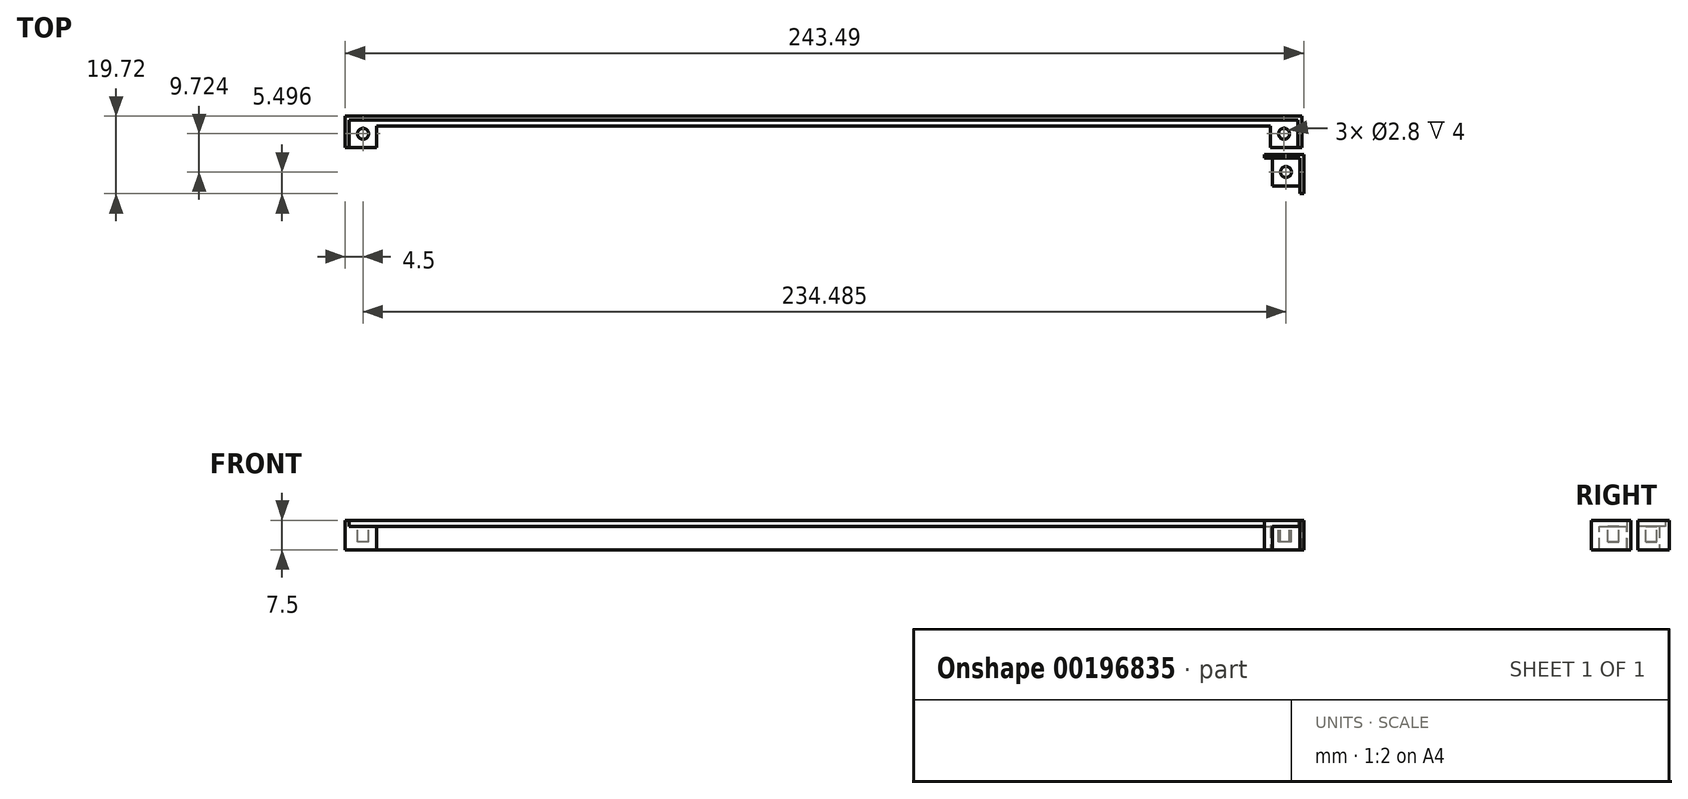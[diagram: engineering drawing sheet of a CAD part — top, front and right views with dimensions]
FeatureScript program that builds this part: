
annotation { "Feature Type Name" : "Feature", "Feature Type Description" : "" }
export const myFeature = defineFeature(function(context is Context, id is Id, definition is map)
    precondition{}
    {
        {
            var Q0;
            Q0=qCreatedBy(makeId("Top.planeOp"),FACE);
            var sketch = newSketch(context, id + "F0", { "sketchPlane" : qUnion([Q0])});
            skLineSegment(sketch, "E0.bottom", {"start": v(121.5, -4) * mm, "end": v(113.5, -4) * mm});
            skLineSegment(sketch, "E0.top", {"start": v(121.5, 4) * mm, "end": v(-121.5, 4) * mm});
            skLineSegment(sketch, "E0.left", {"start": v(121.5, -4) * mm, "end": v(121.5, 4) * mm});
            skLineSegment(sketch, "E0.right", {"start": v(-121.5, -4) * mm, "end": v(-121.5, 4) * mm});
            skPoint(sketch, "E0.middle", {"position": v(0, 0) * mm});
            skLineSegment(sketch, "E1.bottom", {"start": v(-113.5, 1.5) * mm, "end": v(113.5, 1.5) * mm});
            skLineSegment(sketch, "E1.left", {"start": v(-113.5, 1.5) * mm, "end": v(-113.5, -4) * mm});
            skLineSegment(sketch, "E1.right", {"start": v(113.5, 1.5) * mm, "end": v(113.5, -4) * mm});
            skLineSegment(sketch, "E2.trimOffspring", {"start": v(-113.5, -4) * mm, "end": v(-121.5, -4) * mm});
            skSolve(sketch);
        }
        {
            var Q0;
            Q0 = qSketchRegion(id + "F0", true);
            extrude(context, id + "F1", {"entities" : qUnion([Q0]), "depth" : 6 * mm});
        }
        {
            var Q0;
            Q0=makeQuery(id+"F1.opExtrude","CAP_FACE",FACE,{"disambiguationData":[OSD([sQuery(id+"F0.wireOp",EDGE,"E0.bottom"),sQuery(id+"F0.wireOp",EDGE,"E0.top"),sQuery(id+"F0.wireOp",EDGE,"E0.left"),sQuery(id+"F0.wireOp",EDGE,"E0.right")])],"isStart":false});
            var sketch = newSketch(context, id + "F2", { "sketchPlane" : qUnion([Q0])});
            skCircle(sketch, "E3", {"center": v(-117, -0.5) * mm, "radius": 1.4 * mm});
            skCircle(sketch, "E4", {"center": v(117, -0.5) * mm, "radius": 1.4 * mm});
            skSolve(sketch);
        }
        {
            var Q0;
            Q0 = qSketchRegion(id + "F2", true);
            extrude(context, id + "F3", {"entities" : qUnion([Q0]), "operationType" : NewBodyOperationType.REMOVE, "oppositeDirection" : true, "depth" : 4 * mm});
        }
        {
            var Q0;
            Q0=makeQuery(id+"F1.opExtrude","CAP_FACE",FACE,{"disambiguationData":[OSD([sQuery(id+"F0.wireOp",EDGE,"E0.bottom"),sQuery(id+"F0.wireOp",EDGE,"E0.top"),sQuery(id+"F0.wireOp",EDGE,"E0.left"),sQuery(id+"F0.wireOp",EDGE,"E0.right"),sQuery(id+"F0.wireOp",EDGE,"E1.bottom"),sQuery(id+"F0.wireOp",EDGE,"E1.left"),sQuery(id+"F0.wireOp",EDGE,"E1.right"),sQuery(id+"F0.wireOp",EDGE,"E2.trimOffspring")])],"isStart":false});
            var sketch = newSketch(context, id + "F4", { "sketchPlane" : qUnion([Q0])});
            skLineSegment(sketch, "E5", {"start": v(-121.5, 4) * mm, "end": v(-121.5, -4) * mm});
            skLineSegment(sketch, "E6", {"start": v(-121.5, -4) * mm, "end": v(-120.5, -4) * mm});
            skLineSegment(sketch, "E7", {"start": v(-120.5, -4) * mm, "end": v(-120.5, 3) * mm});
            skLineSegment(sketch, "E8", {"start": v(-120.5, 3) * mm, "end": v(120.5, 3) * mm});
            skLineSegment(sketch, "E9", {"start": v(120.5, 3) * mm, "end": v(120.5, -4) * mm});
            skLineSegment(sketch, "E10", {"start": v(120.5, -4) * mm, "end": v(121.5, -4) * mm});
            skLineSegment(sketch, "E11", {"start": v(121.5, -4) * mm, "end": v(121.5, 4) * mm});
            skLineSegment(sketch, "E12", {"start": v(121.5, 4) * mm, "end": v(-121.5, 4) * mm});
            skSolve(sketch);
        }
        {
            var Q0;
            Q0 = qSketchRegion(id + "F4", true);
            extrude(context, id + "F5", {"entities" : qUnion([Q0]), "operationType" : NewBodyOperationType.ADD, "depth" : 1.5 * mm});
        }
        {
            var Q0;
            Q0=qCreatedBy(makeId("Top.planeOp"),FACE);
            var sketch = newSketch(context, id + "F6", { "sketchPlane" : qUnion([Q0])});
            skLineSegment(sketch, "E13.bottom", {"start": v(111.99, -5.72) * mm, "end": v(121.99, -5.72) * mm});
            skLineSegment(sketch, "E13.top", {"start": v(111.99, -15.72) * mm, "end": v(121.99, -15.72) * mm});
            skLineSegment(sketch, "E13.left", {"start": v(111.99, -5.72) * mm, "end": v(111.99, -15.72) * mm});
            skLineSegment(sketch, "E13.right", {"start": v(121.99, -5.72) * mm, "end": v(121.99, -15.72) * mm});
            skSolve(sketch);
        }
        {
            var Q0;
            Q0 = qSketchRegion(id + "F6", true);
            extrude(context, id + "F7", {"entities" : qUnion([Q0]), "depth" : 6 * mm});
        }
        {
            var Q0;
            Q0=makeQuery(id+"F7.opExtrude","CAP_FACE",FACE,{"disambiguationData":[OSD([sQuery(id+"F6.wireOp",EDGE,"E13.bottom"),sQuery(id+"F6.wireOp",EDGE,"E13.top"),sQuery(id+"F6.wireOp",EDGE,"E13.left"),sQuery(id+"F6.wireOp",EDGE,"E13.right")])],"isStart":false});
            var sketch = newSketch(context, id + "F8", { "sketchPlane" : qUnion([Q0])});
            skCircle(sketch, "E14", {"center": v(117.49, -10.22) * mm, "radius": 1.4 * mm});
            skSolve(sketch);
        }
        {
            var Q0;
            Q0 = qSketchRegion(id + "F8", true);
            extrude(context, id + "F9", {"entities" : qUnion([Q0]), "operationType" : NewBodyOperationType.REMOVE, "oppositeDirection" : true, "depth" : 4 * mm});
        }
        {
            var Q0;
            Q0=makeQuery(id+"F7.opExtrude","CAP_FACE",FACE,{"disambiguationData":[OSD([sQuery(id+"F6.wireOp",EDGE,"E13.bottom"),sQuery(id+"F6.wireOp",EDGE,"E13.top"),sQuery(id+"F6.wireOp",EDGE,"E13.left"),sQuery(id+"F6.wireOp",EDGE,"E13.right")])],"isStart":false});
            var sketch = newSketch(context, id + "F10", { "sketchPlane" : qUnion([Q0])});
            skLineSegment(sketch, "E15", {"start": v(111.99, -5.72) * mm, "end": v(121.99, -5.72) * mm});
            skLineSegment(sketch, "E16", {"start": v(121.99, -5.72) * mm, "end": v(121.99, -15.72) * mm});
            skLineSegment(sketch, "E17", {"start": v(121.99, -15.72) * mm, "end": v(120.99, -15.72) * mm});
            skLineSegment(sketch, "E18", {"start": v(120.99, -15.72) * mm, "end": v(120.99, -6.72) * mm});
            skLineSegment(sketch, "E19", {"start": v(120.99, -6.72) * mm, "end": v(111.99, -6.72) * mm});
            skLineSegment(sketch, "E20", {"start": v(111.99, -6.72) * mm, "end": v(111.99, -5.72) * mm});
            skSolve(sketch);
        }
        {
            var Q0;
            Q0 = qSketchRegion(id + "F10", true);
            extrude(context, id + "F11", {"entities" : qUnion([Q0]), "operationType" : NewBodyOperationType.ADD, "depth" : 1.5 * mm});
        }
        {
            var Q0;
            Q0=makeQuery(id+"F7.opExtrude","CAP_FACE",FACE,{"disambiguationData":[OSD([sQuery(id+"F6.wireOp",EDGE,"E13.bottom"),sQuery(id+"F6.wireOp",EDGE,"E13.top"),sQuery(id+"F6.wireOp",EDGE,"E13.left"),sQuery(id+"F6.wireOp",EDGE,"E13.right")])],"isStart":false});
            var sketch = newSketch(context, id + "F12", { "sketchPlane" : qUnion([Q0])});
            skLineSegment(sketch, "E21", {"start": v(111.99, -6.72) * mm, "end": v(111.99, -15.72) * mm});
            skLineSegment(sketch, "E22", {"start": v(111.99, -15.72) * mm, "end": v(120.99, -15.72) * mm});
            skLineSegment(sketch, "E23", {"start": v(120.99, -15.72) * mm, "end": v(120.99, -13.72) * mm});
            skLineSegment(sketch, "E24", {"start": v(120.99, -13.72) * mm, "end": v(113.99, -13.72) * mm});
            skLineSegment(sketch, "E25", {"start": v(113.99, -13.72) * mm, "end": v(113.99, -6.72) * mm});
            skLineSegment(sketch, "E26", {"start": v(113.99, -6.72) * mm, "end": v(111.99, -6.72) * mm});
            skSolve(sketch);
        }
        {
            var Q0;
            Q0 = qSketchRegion(id + "F12", true);
            extrude(context, id + "F13", {"entities" : qUnion([Q0]), "operationType" : NewBodyOperationType.REMOVE, "oppositeDirection" : true, "depth" : 25 * mm});
        }
    });
